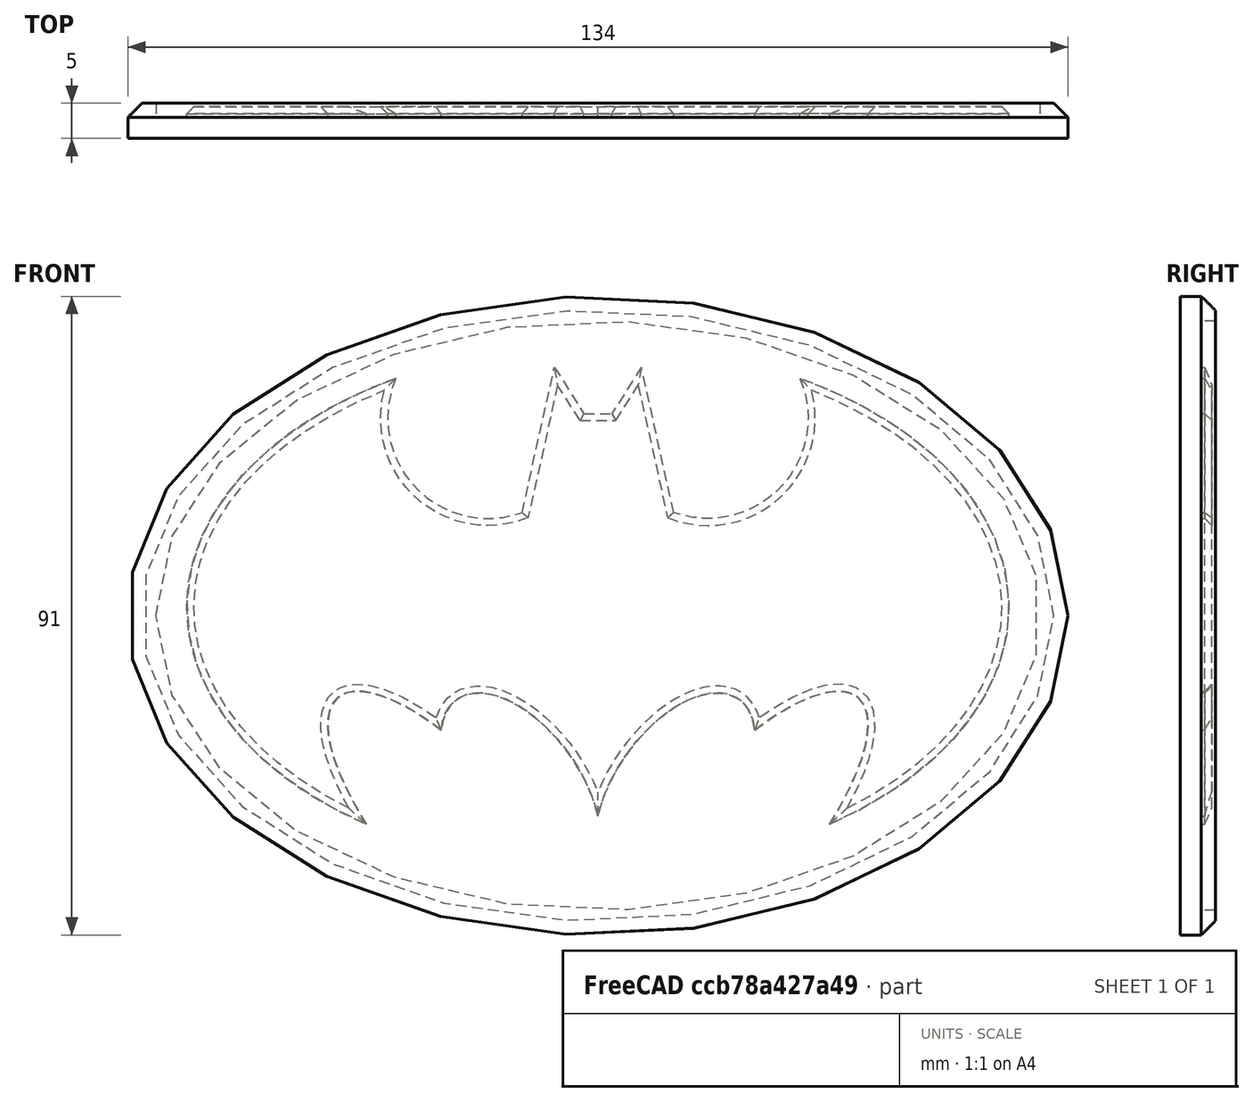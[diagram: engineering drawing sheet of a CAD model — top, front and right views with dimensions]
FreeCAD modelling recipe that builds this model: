
FCSTD DOCUMENT  (FreeCAD 0.16RUnknown)
Label: Logo
License: All rights reserved
LicenseURL: http://en.wikipedia.org/wiki/All_rights_reserved
objects: App::DocumentObjectGroup×3, Sketcher::SketchObject×3, Part::FeaturePython×3, PartDesign::Pad×2, Part::Chamfer×2, Part::MultiFuse×2, Spreadsheet::Sheet×1, Mesh::Feature×1, PartDesign::Pocket×1, Part::Mirroring×1
note: 17 computed .brp shape members not serialized (recipe doc carries the construction recipe); baked Part::Feature solids carry a one-line shape summary decoded from their .brp

FEATURE [Spreadsheet::Sheet] Spreadsheet  label="pars"
  cells = A1=Bolts and Nuts; B1=Value; D1=Components; E1=Value; A2=Thread Tight Tolerance (Radius, ratio); B2(ThrTighRatio)=0.96; D2=Tight Cilinder Tolerances (Radius, mm); E2(CilTight)=0.1; A3=Thread Tight Tolerance (Radius, mm); B3(ThrTightmm)=0.1; D3=Loose Cilinder Tolerances (Radius, mm); E3(CilLoose)=0.1; A5=Nut Slot Width Clearance (mm); B5(NutWidthClearmm)=0.1; A6=Nut Slot Thickess Clearance (mm); B6(NutThickClearmm)=0.1; A13=Particular parameters; B13=Value
FEATURE [Mesh::Feature] Fase2_batman
  Placement = pos=(715,-193.65,-567.5) rot=(-1,0,0;1.5708rad)
FEATURE [App::DocumentObjectGroup] Group  label="Reference"
  Group = -> [Fase2_batman]
FEATURE [Sketcher::SketchObject] Sketch  label="Main"
  Placement = pos=(0,0,0) rot=(-1,0,0;4.71239rad)
  sketch-geometry (5):
    g0: Ellipse CenterX=0 CenterY=0 CenterZ=0 NormalX=0 NormalY=0 NormalZ=1 MajorRadius=67 MinorRadius=45.5 AngleXU=0
    g1: LineSegment [constr] StartX=67 StartY=0 StartZ=0 EndX=-67 EndY=0 EndZ=0
    g2: LineSegment [constr] StartX=0 StartY=45.5 StartZ=0 EndX=0 EndY=-45.5 EndZ=0
    g3: GeomPoint [constr] X=49.1808 Y=0 Z=0
    g4: GeomPoint [constr] X=-49.1808 Y=0 Z=0
  constraints (5):
    c: InternalAlignment(g1-g4 -> g0) x4
    c: Coincident(g0,g-1)
    c: Horizontal(g1)
    c: DistanceX(g1,g1) = 134
    c: DistanceY(g2,g2) = 91
FEATURE [PartDesign::Pad] Pad  label="MainPad"
  Length = 5
  Length2 = 100
  Placement = pos=(0,0,0) rot=(-1,0,0;4.71239rad)
  Reversed = true
  Sketch = -> Sketch
  Type = 0
FEATURE [Part::Chamfer] Chamfer  label="MainChamfer"
  Base = -> Pad
  Edges = 1 edges r=2: [Edge3]
FEATURE [Sketcher::SketchObject] Sketch001  label="MainPocket"
  Placement = pos=(0,5,0) rot=(0,0.707107,0.707107;3.14159rad)
  Support = -> Chamfer [Face4]
  sketch-geometry (5):
    g0: Ellipse CenterX=0 CenterY=0 CenterZ=0 NormalX=0 NormalY=0 NormalZ=1 MajorRadius=63 MinorRadius=42 AngleXU=0
    g1: LineSegment [constr] StartX=63 StartY=0 StartZ=0 EndX=-63 EndY=0 EndZ=0
    g2: LineSegment [constr] StartX=0 StartY=42 StartZ=0 EndX=0 EndY=-42 EndZ=0
    g3: GeomPoint [constr] X=46.9574 Y=0 Z=0
    g4: GeomPoint [constr] X=-46.9574 Y=0 Z=0
  constraints (5):
    c: InternalAlignment(g1-g4 -> g0) x4
    c: Coincident(g0,g-1)
    c: Horizontal(g1)
    c: DistanceX(g1,g1) = 126
    c: DistanceY(g2,g2) = 84
FEATURE [PartDesign::Pocket] Pocket  label="MainPocket001"
  Length = 2
  Sketch = -> Sketch001
  Type = 0
FEATURE [Sketcher::SketchObject] Sketch002  label="BatmanMain"
  Placement = pos=(0,0,0) rot=(0,0.707107,0.707107;3.14159rad)
  sketch-geometry (24):
    g0: LineSegment StartX=0 StartY=28.8 StartZ=0 EndX=2 EndY=28.8 EndZ=0
    g1: LineSegment StartX=2 StartY=28.8 StartZ=0 EndX=6.2 EndY=35.4 EndZ=0
    g2: LineSegment StartX=6.2 StartY=35.4 StartZ=0 EndX=10.8 EndY=14.7 EndZ=0
    g3: LineSegment StartX=0 StartY=28.8 StartZ=0 EndX=0 EndY=-28.6 EndZ=0
    g4: ArcOfEllipse CenterX=11.0282 CenterY=-24.4835 CenterZ=0 NormalX=0 NormalY=0 NormalZ=1 MajorRadius=15.5 MinorRadius=8.4 AngleXU=0.942478 StartAngle=5.74005 EndAngle=8.53949
    g5: LineSegment [constr] StartX=20.1389 StartY=-11.9437 StartZ=0 EndX=1.91756 EndY=-37.0233 EndZ=0
    g6: LineSegment [constr] StartX=4.23249 StartY=-19.5461 StartZ=0 EndX=17.824 EndY=-29.4209 EndZ=0
    g7: GeomPoint [constr] X=18.685 Y=-13.9448 Z=0
    g8: GeomPoint [constr] X=3.37144 Y=-35.0222 Z=0
    g9: ArcOfEllipse CenterX=19.4066 CenterY=-32.0947 CenterZ=0 NormalX=0 NormalY=0 NormalZ=1 MajorRadius=27 MinorRadius=9.47714 AngleXU=0.856201 StartAngle=5.12054 EndAngle=7.31522
    g10: LineSegment [constr] StartX=37.1 StartY=-11.7 StartZ=0 EndX=1.71318 EndY=-52.4894 EndZ=0
    g11: LineSegment [constr] StartX=12.2479 StartY=-25.8842 StartZ=0 EndX=26.5652 EndY=-38.3052 EndZ=0
    g12: GeomPoint [constr] X=35.9742 Y=-12.9976 Z=0
    g13: GeomPoint [constr] X=2.83895 Y=-51.1917 Z=0
    g14: ArcOfEllipse CenterX=0 CenterY=1.21691 CenterZ=0 NormalX=0 NormalY=0 NormalZ=1 MajorRadius=58.6 MinorRadius=37.4133 AngleXU=0 StartAngle=5.31057 EndAngle=7.34021
    g15: LineSegment [constr] StartX=58.6 StartY=1.21691 StartZ=0 EndX=-58.6 EndY=1.21691 EndZ=0
    g16: LineSegment [constr] StartX=0 StartY=38.6302 StartZ=0 EndX=0 EndY=-36.1964 EndZ=0
    g17: GeomPoint [constr] X=45.1022 Y=1.21691 Z=0
    g18: GeomPoint [constr] X=-45.1022 Y=1.21691 Z=0
    g19: ArcOfEllipse CenterX=15.6648 CenterY=28.1471 CenterZ=0 NormalX=0 NormalY=0 NormalZ=1 MajorRadius=14.3 MinorRadius=14.3 AngleXU=-0.610865 StartAngle=4.97613 EndAngle=7.30045
    g20: LineSegment [constr] StartX=27.3786 StartY=19.9449 StartZ=0 EndX=3.95088 EndY=36.3492 EndZ=0
    g21: LineSegment [constr] StartX=23.8669 StartY=39.861 StartZ=0 EndX=7.46262 EndY=16.4332 EndZ=0
    g22: GeomPoint [constr] X=15.6648 Y=28.147 Z=0
    g23: GeomPoint [constr] X=15.6647 Y=28.1471 Z=0
  constraints (39):
    c: Coincident(g0,g1)
    c: Coincident(g1,g2)
    c: Horizontal(g0)
    c: Vertical(g3)
    c: Coincident(g0,g3)
    c: InternalAlignment(g5-g8 -> g4) x4
    c: Coincident(g3,g4)
    c: PointOnObject(g3,g-2)
    c: DistanceY(g3) = -28.6
    c: DistanceX(g4) = 22.34
    c: DistanceY(g4) = -16.3
    c: InternalAlignment(g10-g13 -> g9) x4
    c: Coincident(g4,g9)
    c: DistanceX(g9) = 33
    c: DistanceY(g9) = -29.7
    c: InternalAlignment(g15-g18 -> g14) x4
    c: PointOnObject(g14,g3)
    c: Horizontal(g15)
    c: Coincident(g9,g14)
    c: DistanceX(g14) = 28.8
    c: DistanceY(g14) = 33.8
    c: DistanceY(g0) = 28.8
    c: DistanceX(g0,g0) = 2
    c: DistanceX(g1) = 6.2
    c: DistanceY(g1) = 35.4
    c: InternalAlignment(g20-g23 -> g19) x4
    c: Coincident(g19,g14)
    c: DistanceX(g2) = 10.8
    c: DistanceY(g2) = 14.7
    c: Coincident(g2,g19)
    c: Angle(g5) = -2.19911
    c: Distance(g5) = 31
    c: Distance(g6) = 16.8
    c: DistanceY(g10) = -11.7
    c: DistanceX(g10) = 37.1
    c: Distance(g10) = 54
    c: DistanceX(g15) = 58.6
    c: Angle(g20) = 2.53073
    c: Distance(g20) = 28.6
FEATURE [PartDesign::Pad] Pad001  label="BatmanMain001"
  Length = 2
  Length2 = 100
  Placement = pos=(0,0,0) rot=(0,0.707107,0.707107;3.14159rad)
  Sketch = -> Sketch002
  Type = 0
FEATURE [Part::Chamfer] Chamfer001  label="BatChamfer"
  Base = -> Pad001
  Edges = 7 edges r=1: [Edge4,Edge7,Edge10,Edge13,Edge16,Edge19,Edge22]
FEATURE [Part::Mirroring] Part__Mirroring  label="BatChamfer (Mirror #1)"
  Base = (0,0,0)
  Normal = (1,0,0)
  Source = -> Chamfer001
FEATURE [Part::MultiFuse] Fusion  label="BatMirror"
  Shapes = -> [Part__Mirroring,Chamfer001]
FEATURE [Part::FeaturePython] refine  label="Batman"  # WARN: FeaturePython — macro-defined, semantics opaque (R4)
  Base = -> Fusion
FEATURE [App::DocumentObjectGroup] Group002  label="Batman_src"
  Group = -> [Pad001,Fusion,refine]
FEATURE [Part::FeaturePython] Clone  label="Clone of Batman oh no"  # Draft clone (typed FeaturePython)
  Objects = -> [refine]
  Placement = pos=(0,2.5,0) rot=(0,0,1;0rad)
  Scale = (1,1,1)
FEATURE [Part::MultiFuse] Fusion001  label="BatAdd"
  Shapes = -> [Pocket,Clone]
FEATURE [App::DocumentObjectGroup] Group001  label="src"
  Group = -> [Pad,Chamfer,Fusion001]
FEATURE [Part::FeaturePython] Clone001  label="Logo"  # Draft clone (typed FeaturePython)
  Objects = -> [Fusion001]
  Scale = (1,1,1)
